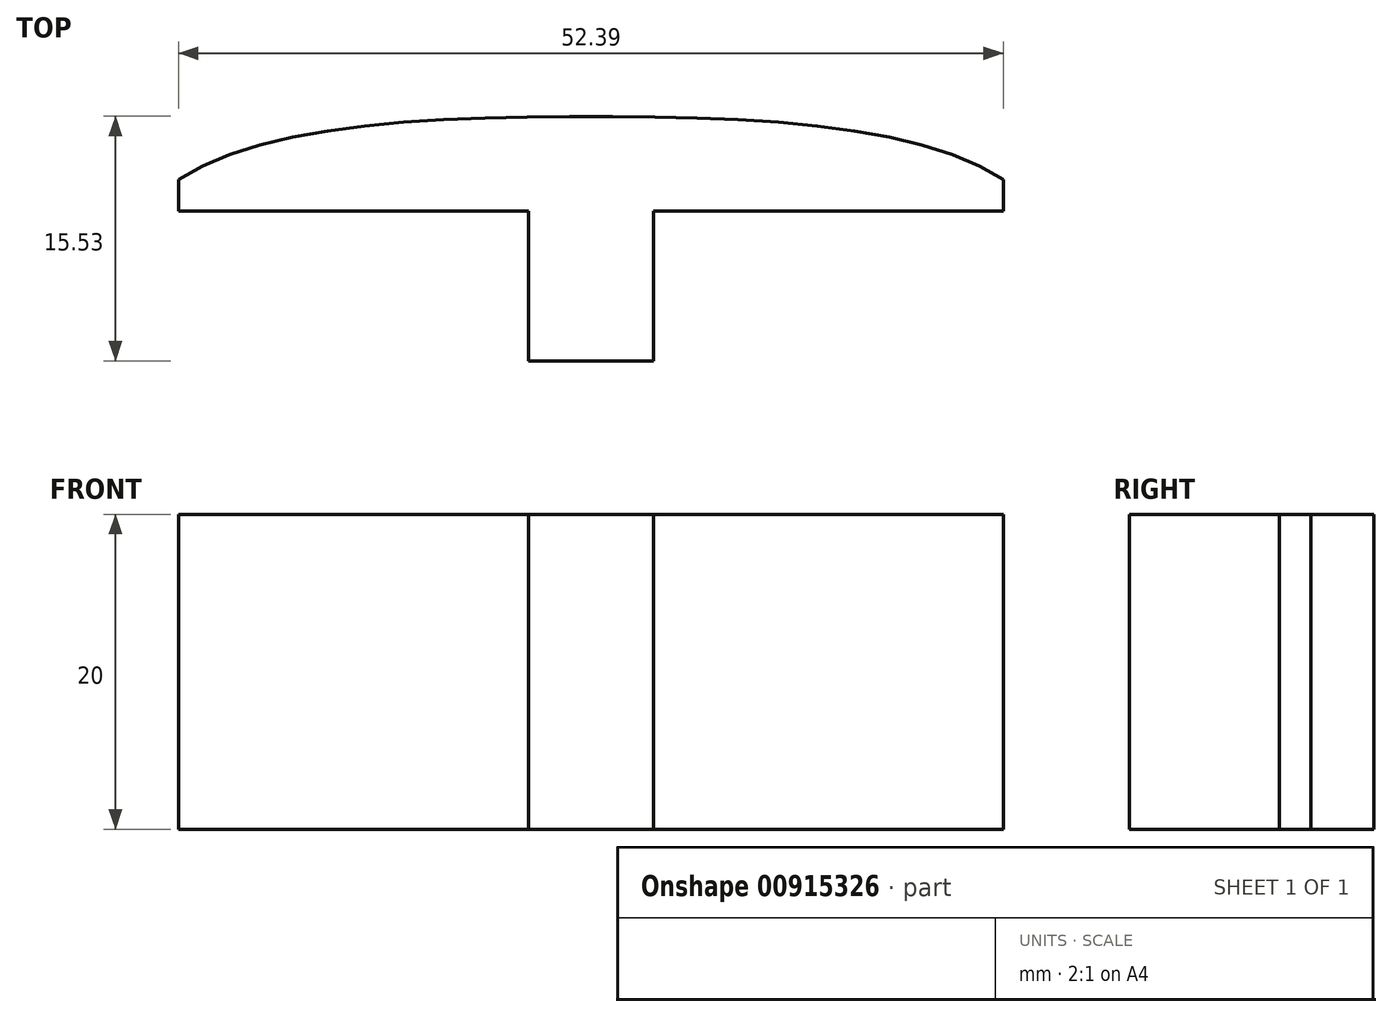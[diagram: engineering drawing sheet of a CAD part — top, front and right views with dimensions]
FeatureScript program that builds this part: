
annotation { "Feature Type Name" : "Feature", "Feature Type Description" : "" }
export const myFeature = defineFeature(function(context is Context, id is Id, definition is map)
    precondition{}
    {
        {
            var Q0;
            Q0=qCreatedBy(makeId("Top.planeOp"),FACE);
            var sketch = newSketch(context, id + "F0", { "sketchPlane" : qUnion([Q0])});
            skLineSegment(sketch, "E0", {"start": v(0, 0) * mm, "end": v(7.94, 0) * mm});
            skLineSegment(sketch, "E1", {"start": v(7.94, 0) * mm, "end": v(7.94, 9.53) * mm});
            skLineSegment(sketch, "E2", {"start": v(7.94, 9.53) * mm, "end": v(30.16, 9.53) * mm});
            skLineSegment(sketch, "E3", {"start": v(30.16, 9.52) * mm, "end": v(30.16, 11.53) * mm});
            skLineSegment(sketch, "E4", {"start": v(0, 0) * mm, "end": v(0, 9.53) * mm});
            skLineSegment(sketch, "E5", {"start": v(0, 9.53) * mm, "end": v(-22.23, 9.52) * mm});
            skLineSegment(sketch, "E6", {"start": v(-22.23, 9.52) * mm, "end": v(-22.23, 11.53) * mm});
            skFitSpline(sketch, "E7", {"points": [v(-22.23, 11.53) * mm, v(3.97, 15.52) * mm, v(30.16, 11.53) * mm], "startDerivative": vector(32.43, 21.1) * mm, "endDerivative": vector(32.43, -21.1) * mm});
            skLineSegment(sketch, "E8", {"start": v(0, 9.53) * mm, "end": v(7.94, 9.53) * mm, "construction": true});
            skLineSegment(sketch, "E9", {"start": v(3.97, 9.53) * mm, "end": v(3.97, 15.52) * mm, "construction": true});
            skSolve(sketch);
        }
        {
            var Q0;
            Q0=makeQuery(id+"F0.imprint","IMPRINT",FACE,{"disambiguationData":[TD([[makeQuery(id+"F0.imprint","IMPRINT",EDGE,{"derivedFrom":sQuery(id+"F0.wireOp",EDGE,"E0")}),1.0]])]});
            extrude(context, id + "F1", {"entities" : qUnion([Q0]), "depth" : 20 * mm, "offsetDistance" : 25 * mm});
        }
    });
